# Revit family: BIMLIB_Конвектор_Мебельный_ВКВМ090_VITRON
name_source: partatom
category: Оборудование
revit_build: Autodesk Revit 2017 (Build: 20190508_0315(x64)
units: mm (PartAtom-declared; Revit-internal decimal feet)

## family parameters
Всегда вертикально = Да
На основе рабочей плоскости = Нет
Общий = Нет
При загрузке вырезать с полостями = Нет
Размер круглого соединителя = Использовать диаметр
Тип детали = Нормальный
Точка расчета площади = Нет

## types (1)
- Конвектор_Шириной 335мм
    1 = 1
    2 = 2
    3 = 3
    ADSK_URL документации изделия = https://vitron.ru
    ADSK_URL страницы изделия = https://vitron.ru
    ADSK_Версия Revit = 2017
    ADSK_Единица измерения = шт.
    ADSK_Завод-изготовитель = Вилма / VITRON
    ADSK_Классификация нагрузок = Прочее
    ADSK_Количество фаз = 1
    ADSK_Коэффициент мощности = 0.98
    ADSK_Обозначение = ВКВМ.090.335
    ADSK_Размер_Высота = 90 мм
    ADSK_Размер_Диаметр = 15 мм
    ADSK_Размер_Ширина = 335 мм
    BL_BIM library = https://bimlib.pro
    URL = https://vitron.ru
    VIT_Максимальная рабочая температура теплоносителя = 95 °C
    VIT_Рабочее давление теплоносителя = 1600000.0 Па
    VIT_Степень защиты вентилятора = IP20
    VIT_Тепловая мощность на 1 м = 2153.333 Вт
    VIT_Уровень звукового давления от вентилятора = 19/30 дБ(А)
    Высота теплообменника = 50 мм
    Изготовитель = Вилма / VITRON
    Количество труб теплообменника = 4
    Коэффициент n = 1.3
    Материал_Корпуса = BIMLIB_ОцинкованнаяСтальЧерная_VITRON
    Материал_Решетка = BIMLIB_Алюминий_VITRON
    Описание = Встраиваемый в мебель конвектор с принудительной конвекцией VITRON - отопительный прибор, в котором установлен медно-алюминиевый теплообменник и тангенциальный вентилятор, тепло от которого передаётся в отапливаемое помещение путём
естественной (при выключенном вентиляторе), и принудительной (при включенном вентиляторе) конвекции. Предназначен для отопления кухонных помещений и вестибюлей.
Данный конвектор можно располагать в шкафах, лестничных ступеньках под тумбами
и кухонной мебелью. Может быть установлен как в однотрубную, так и в двухтрубную
систему отопления. Рекомендуется применять только в насосных системах отопления.
Данный тип конвектора служит для отопления сухих помещений.
    Расстояние между патрубками = 150 мм
    Ширина теплообменника = 200 мм
